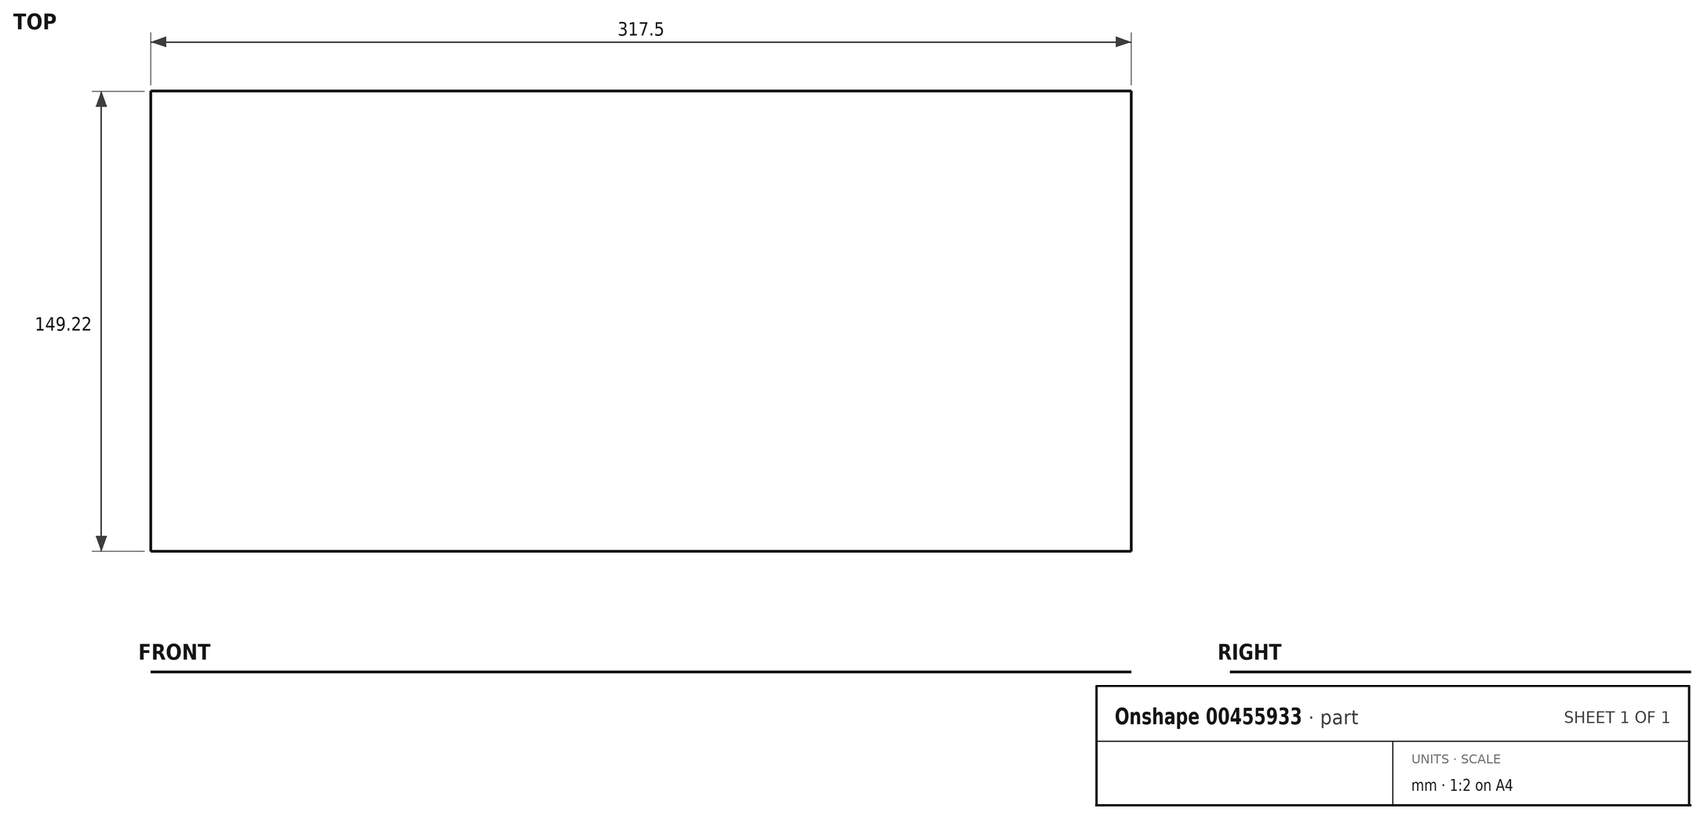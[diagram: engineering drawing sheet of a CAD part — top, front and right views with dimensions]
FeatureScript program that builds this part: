
annotation { "Feature Type Name" : "Feature", "Feature Type Description" : "" }
export const myFeature = defineFeature(function(context is Context, id is Id, definition is map)
    precondition{}
    {
        {
            var Q0;
            Q0=qCreatedBy(makeId("Top.planeOp"),FACE);
            var sketch = newSketch(context, id + "F0", { "sketchPlane" : qUnion([Q0])});
            skLineSegment(sketch, "E0.bottom", {"start": v(158.75, -74.61) * mm, "end": v(-158.75, -74.61) * mm});
            skLineSegment(sketch, "E0.top", {"start": v(158.75, 74.61) * mm, "end": v(-158.75, 74.61) * mm});
            skLineSegment(sketch, "E0.left", {"start": v(158.75, -74.61) * mm, "end": v(158.75, 74.61) * mm});
            skLineSegment(sketch, "E0.right", {"start": v(-158.75, -74.61) * mm, "end": v(-158.75, 74.61) * mm});
            skPoint(sketch, "E0.middle", {"position": v(0, 0) * mm});
            skSolve(sketch);
        }
        {
            var Q0;
            Q0=makeQuery(id+"F0.imprint","IMPRINT",FACE,{"disambiguationData":[TD([[makeQuery(id+"F0.imprint","IMPRINT",EDGE,{"derivedFrom":sQuery(id+"F0.wireOp",EDGE,"E0.bottom")}),-1.0]])]});
            extrude(context, id + "F1", {"entities" : qUnion([Q0]), "depth" : 1 / 812.8 * mm});
        }
    });
